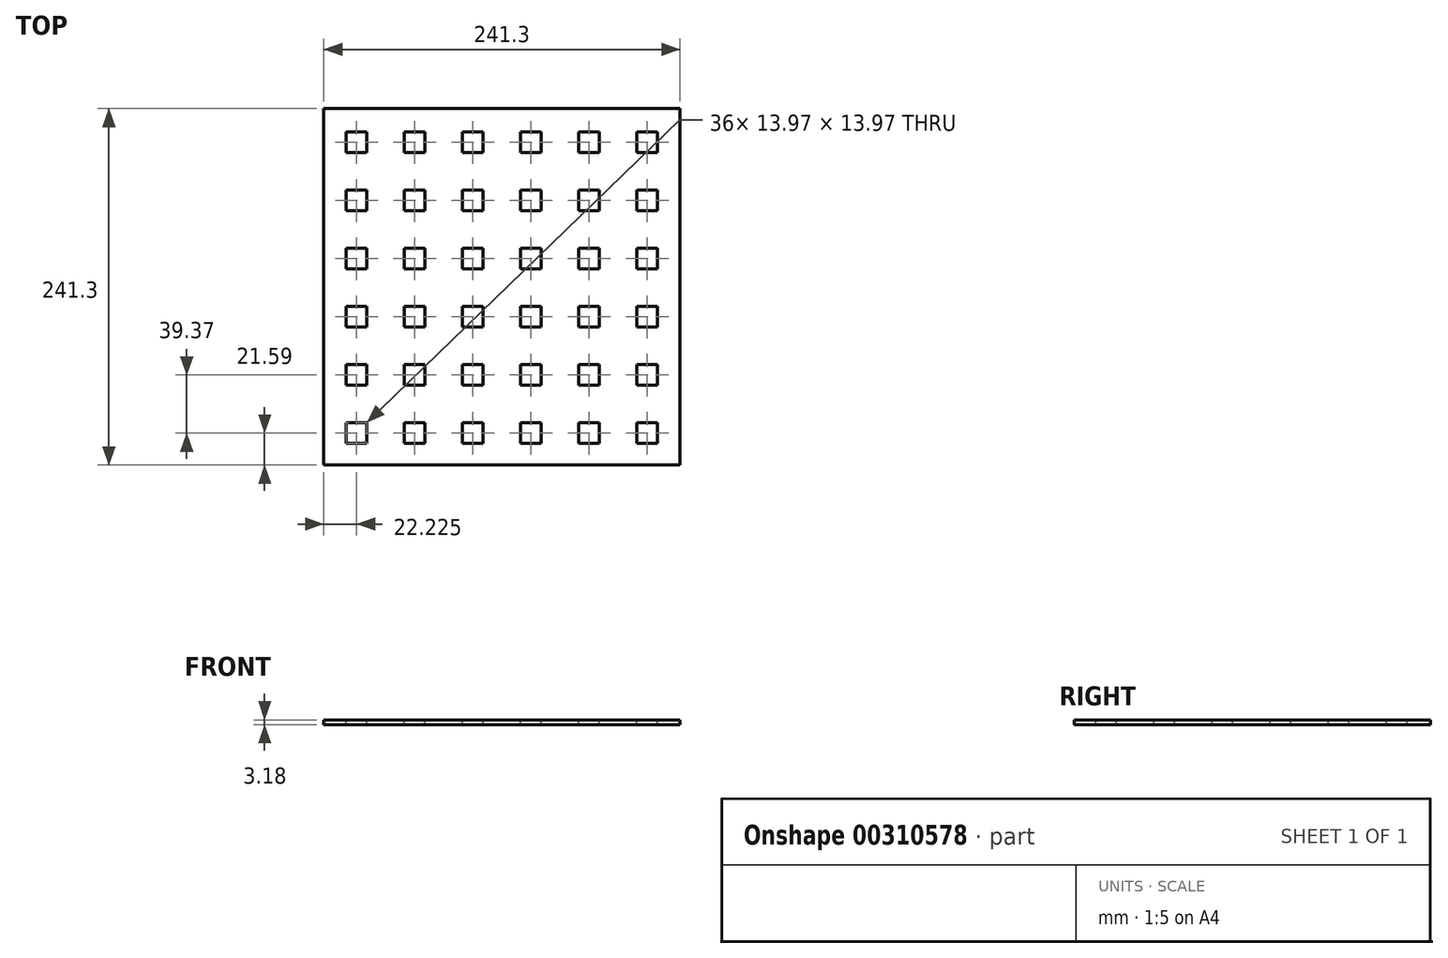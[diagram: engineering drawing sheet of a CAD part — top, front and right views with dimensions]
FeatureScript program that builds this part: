
annotation { "Feature Type Name" : "Feature", "Feature Type Description" : "" }
export const myFeature = defineFeature(function(context is Context, id is Id, definition is map)
    precondition{}
    {
        {
            var Q0;
            Q0=qCreatedBy(makeId("Top.planeOp"),FACE);
            var sketch = newSketch(context, id + "F0", { "sketchPlane" : qUnion([Q0])});
            skLineSegment(sketch, "E0.bottom", {"start": v(120.65, 120.65) * mm, "end": v(-120.65, 120.65) * mm});
            skLineSegment(sketch, "E0.top", {"start": v(120.65, -120.65) * mm, "end": v(-120.65, -120.65) * mm});
            skLineSegment(sketch, "E0.left", {"start": v(120.65, 120.65) * mm, "end": v(120.65, -120.65) * mm});
            skLineSegment(sketch, "E0.right", {"start": v(-120.65, 120.65) * mm, "end": v(-120.65, -120.65) * mm});
            skPoint(sketch, "E0.middle", {"position": v(0, 0) * mm});
            skSolve(sketch);
        }
        {
            var Q0;
            Q0=makeQuery(id+"F0.imprint","IMPRINT",FACE,{"disambiguationData":[TD([[makeQuery(id+"F0.imprint","IMPRINT",EDGE,{"derivedFrom":sQuery(id+"F0.wireOp",EDGE,"E0.bottom")}),1.0]])]});
            extrude(context, id + "F1", {"entities" : qUnion([Q0]), "depth" : 3.17 * mm, "symmetric" : true});
        }
        {
            var Q0;
            Q0=makeQuery(id+"F1.opExtrude","CAP_FACE",FACE,{"disambiguationData":[OSD([sQuery(id+"F0.wireOp",EDGE,"E0.bottom"),sQuery(id+"F0.wireOp",EDGE,"E0.top"),sQuery(id+"F0.wireOp",EDGE,"E0.left"),sQuery(id+"F0.wireOp",EDGE,"E0.right")])],"isStart":false});
            var sketch = newSketch(context, id + "F2", { "sketchPlane" : qUnion([Q0])});
            skLineSegment(sketch, "E1.bottom", {"start": v(-91.44, 104.78) * mm, "end": v(-105.41, 104.78) * mm});
            skLineSegment(sketch, "E1.top", {"start": v(-91.44, 90.8) * mm, "end": v(-105.41, 90.8) * mm});
            skLineSegment(sketch, "E1.left", {"start": v(-91.44, 104.78) * mm, "end": v(-91.44, 90.8) * mm});
            skLineSegment(sketch, "E1.right", {"start": v(-105.41, 104.78) * mm, "end": v(-105.41, 90.8) * mm});
            skPoint(sketch, "E1.middle", {"position": v(-98.43, 97.8) * mm});
            skLineSegment(sketch, "E2.0.1.0", {"start": v(-105.41, 65.4) * mm, "end": v(-105.41, 51.44) * mm});
            skLineSegment(sketch, "E2.0.1.1", {"start": v(-91.44, 65.4) * mm, "end": v(-105.41, 65.4) * mm});
            skLineSegment(sketch, "E2.0.1.2", {"start": v(-91.44, 65.4) * mm, "end": v(-91.44, 51.44) * mm});
            skLineSegment(sketch, "E2.0.1.3", {"start": v(-91.44, 51.44) * mm, "end": v(-105.41, 51.44) * mm});
            skLineSegment(sketch, "E2.0.2.0", {"start": v(-105.41, 26.04) * mm, "end": v(-105.41, 12.07) * mm});
            skLineSegment(sketch, "E2.0.2.1", {"start": v(-91.44, 26.04) * mm, "end": v(-105.41, 26.04) * mm});
            skLineSegment(sketch, "E2.0.2.2", {"start": v(-91.44, 26.04) * mm, "end": v(-91.44, 12.07) * mm});
            skLineSegment(sketch, "E2.0.2.3", {"start": v(-91.44, 12.07) * mm, "end": v(-105.41, 12.07) * mm});
            skLineSegment(sketch, "E2.0.3.0", {"start": v(-105.41, -13.33) * mm, "end": v(-105.41, -27.3) * mm});
            skLineSegment(sketch, "E2.0.3.1", {"start": v(-91.44, -13.33) * mm, "end": v(-105.41, -13.33) * mm});
            skLineSegment(sketch, "E2.0.3.2", {"start": v(-91.44, -13.33) * mm, "end": v(-91.44, -27.3) * mm});
            skLineSegment(sketch, "E2.0.3.3", {"start": v(-91.44, -27.3) * mm, "end": v(-105.41, -27.3) * mm});
            skLineSegment(sketch, "E2.0.4.0", {"start": v(-105.41, -52.7) * mm, "end": v(-105.41, -66.67) * mm});
            skLineSegment(sketch, "E2.0.4.1", {"start": v(-91.44, -52.7) * mm, "end": v(-105.41, -52.7) * mm});
            skLineSegment(sketch, "E2.0.4.2", {"start": v(-91.44, -52.7) * mm, "end": v(-91.44, -66.67) * mm});
            skLineSegment(sketch, "E2.0.4.3", {"start": v(-91.44, -66.67) * mm, "end": v(-105.41, -66.67) * mm});
            skLineSegment(sketch, "E2.0.5.0", {"start": v(-105.41, -92.07) * mm, "end": v(-105.41, -106.04) * mm});
            skLineSegment(sketch, "E2.0.5.1", {"start": v(-91.44, -92.07) * mm, "end": v(-105.41, -92.07) * mm});
            skLineSegment(sketch, "E2.0.5.2", {"start": v(-91.44, -92.07) * mm, "end": v(-91.44, -106.04) * mm});
            skLineSegment(sketch, "E2.0.5.3", {"start": v(-91.44, -106.05) * mm, "end": v(-105.41, -106.05) * mm});
            skLineSegment(sketch, "E2.1.0.0", {"start": v(-66.04, 104.78) * mm, "end": v(-66.04, 90.8) * mm});
            skLineSegment(sketch, "E2.1.0.1", {"start": v(-52.07, 104.78) * mm, "end": v(-66.04, 104.78) * mm});
            skLineSegment(sketch, "E2.1.0.2", {"start": v(-52.07, 104.78) * mm, "end": v(-52.07, 90.8) * mm});
            skLineSegment(sketch, "E2.1.0.3", {"start": v(-52.07, 90.8) * mm, "end": v(-66.04, 90.8) * mm});
            skLineSegment(sketch, "E2.1.1.0", {"start": v(-66.04, 65.4) * mm, "end": v(-66.04, 51.44) * mm});
            skLineSegment(sketch, "E2.1.1.1", {"start": v(-52.07, 65.4) * mm, "end": v(-66.04, 65.4) * mm});
            skLineSegment(sketch, "E2.1.1.2", {"start": v(-52.07, 65.4) * mm, "end": v(-52.07, 51.44) * mm});
            skLineSegment(sketch, "E2.1.1.3", {"start": v(-52.07, 51.44) * mm, "end": v(-66.04, 51.44) * mm});
            skLineSegment(sketch, "E2.1.2.0", {"start": v(-66.04, 26.04) * mm, "end": v(-66.04, 12.07) * mm});
            skLineSegment(sketch, "E2.1.2.1", {"start": v(-52.07, 26.04) * mm, "end": v(-66.04, 26.04) * mm});
            skLineSegment(sketch, "E2.1.2.2", {"start": v(-52.07, 26.04) * mm, "end": v(-52.07, 12.07) * mm});
            skLineSegment(sketch, "E2.1.2.3", {"start": v(-52.07, 12.07) * mm, "end": v(-66.04, 12.07) * mm});
            skLineSegment(sketch, "E2.1.3.0", {"start": v(-66.04, -13.33) * mm, "end": v(-66.04, -27.3) * mm});
            skLineSegment(sketch, "E2.1.3.1", {"start": v(-52.07, -13.33) * mm, "end": v(-66.04, -13.33) * mm});
            skLineSegment(sketch, "E2.1.3.2", {"start": v(-52.07, -13.33) * mm, "end": v(-52.07, -27.3) * mm});
            skLineSegment(sketch, "E2.1.3.3", {"start": v(-52.07, -27.3) * mm, "end": v(-66.04, -27.3) * mm});
            skLineSegment(sketch, "E2.1.4.0", {"start": v(-66.04, -52.7) * mm, "end": v(-66.04, -66.67) * mm});
            skLineSegment(sketch, "E2.1.4.1", {"start": v(-52.07, -52.7) * mm, "end": v(-66.04, -52.7) * mm});
            skLineSegment(sketch, "E2.1.4.2", {"start": v(-52.07, -52.7) * mm, "end": v(-52.07, -66.67) * mm});
            skLineSegment(sketch, "E2.1.4.3", {"start": v(-52.07, -66.67) * mm, "end": v(-66.04, -66.67) * mm});
            skLineSegment(sketch, "E2.1.5.0", {"start": v(-66.04, -92.07) * mm, "end": v(-66.04, -106.04) * mm});
            skLineSegment(sketch, "E2.1.5.1", {"start": v(-52.07, -92.07) * mm, "end": v(-66.04, -92.07) * mm});
            skLineSegment(sketch, "E2.1.5.2", {"start": v(-52.07, -92.07) * mm, "end": v(-52.07, -106.04) * mm});
            skLineSegment(sketch, "E2.1.5.3", {"start": v(-52.07, -106.05) * mm, "end": v(-66.04, -106.05) * mm});
            skLineSegment(sketch, "E2.2.0.0", {"start": v(-26.67, 104.78) * mm, "end": v(-26.67, 90.8) * mm});
            skLineSegment(sketch, "E2.2.0.1", {"start": v(-12.7, 104.78) * mm, "end": v(-26.67, 104.78) * mm});
            skLineSegment(sketch, "E2.2.0.2", {"start": v(-12.7, 104.78) * mm, "end": v(-12.7, 90.8) * mm});
            skLineSegment(sketch, "E2.2.0.3", {"start": v(-12.7, 90.8) * mm, "end": v(-26.67, 90.8) * mm});
            skLineSegment(sketch, "E2.2.1.0", {"start": v(-26.67, 65.4) * mm, "end": v(-26.67, 51.44) * mm});
            skLineSegment(sketch, "E2.2.1.1", {"start": v(-12.7, 65.4) * mm, "end": v(-26.67, 65.4) * mm});
            skLineSegment(sketch, "E2.2.1.2", {"start": v(-12.7, 65.4) * mm, "end": v(-12.7, 51.44) * mm});
            skLineSegment(sketch, "E2.2.1.3", {"start": v(-12.7, 51.44) * mm, "end": v(-26.67, 51.44) * mm});
            skLineSegment(sketch, "E2.2.2.0", {"start": v(-26.67, 26.04) * mm, "end": v(-26.67, 12.07) * mm});
            skLineSegment(sketch, "E2.2.2.1", {"start": v(-12.7, 26.04) * mm, "end": v(-26.67, 26.04) * mm});
            skLineSegment(sketch, "E2.2.2.2", {"start": v(-12.7, 26.04) * mm, "end": v(-12.7, 12.07) * mm});
            skLineSegment(sketch, "E2.2.2.3", {"start": v(-12.7, 12.07) * mm, "end": v(-26.67, 12.07) * mm});
            skLineSegment(sketch, "E2.2.3.0", {"start": v(-26.67, -13.33) * mm, "end": v(-26.67, -27.3) * mm});
            skLineSegment(sketch, "E2.2.3.1", {"start": v(-12.7, -13.33) * mm, "end": v(-26.67, -13.33) * mm});
            skLineSegment(sketch, "E2.2.3.2", {"start": v(-12.7, -13.33) * mm, "end": v(-12.7, -27.3) * mm});
            skLineSegment(sketch, "E2.2.3.3", {"start": v(-12.7, -27.3) * mm, "end": v(-26.67, -27.3) * mm});
            skLineSegment(sketch, "E2.2.4.0", {"start": v(-26.67, -52.7) * mm, "end": v(-26.67, -66.67) * mm});
            skLineSegment(sketch, "E2.2.4.1", {"start": v(-12.7, -52.7) * mm, "end": v(-26.67, -52.7) * mm});
            skLineSegment(sketch, "E2.2.4.2", {"start": v(-12.7, -52.7) * mm, "end": v(-12.7, -66.67) * mm});
            skLineSegment(sketch, "E2.2.4.3", {"start": v(-12.7, -66.67) * mm, "end": v(-26.67, -66.67) * mm});
            skLineSegment(sketch, "E2.2.5.0", {"start": v(-26.67, -92.07) * mm, "end": v(-26.67, -106.04) * mm});
            skLineSegment(sketch, "E2.2.5.1", {"start": v(-12.7, -92.07) * mm, "end": v(-26.67, -92.07) * mm});
            skLineSegment(sketch, "E2.2.5.2", {"start": v(-12.7, -92.07) * mm, "end": v(-12.7, -106.04) * mm});
            skLineSegment(sketch, "E2.2.5.3", {"start": v(-12.7, -106.05) * mm, "end": v(-26.67, -106.05) * mm});
            skLineSegment(sketch, "E2.3.0.0", {"start": v(12.7, 104.78) * mm, "end": v(12.7, 90.8) * mm});
            skLineSegment(sketch, "E2.3.0.1", {"start": v(26.67, 104.78) * mm, "end": v(12.7, 104.78) * mm});
            skLineSegment(sketch, "E2.3.0.2", {"start": v(26.67, 104.78) * mm, "end": v(26.67, 90.8) * mm});
            skLineSegment(sketch, "E2.3.0.3", {"start": v(26.67, 90.8) * mm, "end": v(12.7, 90.8) * mm});
            skLineSegment(sketch, "E2.3.1.0", {"start": v(12.7, 65.4) * mm, "end": v(12.7, 51.44) * mm});
            skLineSegment(sketch, "E2.3.1.1", {"start": v(26.67, 65.4) * mm, "end": v(12.7, 65.4) * mm});
            skLineSegment(sketch, "E2.3.1.2", {"start": v(26.67, 65.4) * mm, "end": v(26.67, 51.44) * mm});
            skLineSegment(sketch, "E2.3.1.3", {"start": v(26.67, 51.44) * mm, "end": v(12.7, 51.44) * mm});
            skLineSegment(sketch, "E2.3.2.0", {"start": v(12.7, 26.04) * mm, "end": v(12.7, 12.07) * mm});
            skLineSegment(sketch, "E2.3.2.1", {"start": v(26.67, 26.04) * mm, "end": v(12.7, 26.04) * mm});
            skLineSegment(sketch, "E2.3.2.2", {"start": v(26.67, 26.04) * mm, "end": v(26.67, 12.07) * mm});
            skLineSegment(sketch, "E2.3.2.3", {"start": v(26.67, 12.07) * mm, "end": v(12.7, 12.07) * mm});
            skLineSegment(sketch, "E2.3.3.0", {"start": v(12.7, -13.33) * mm, "end": v(12.7, -27.3) * mm});
            skLineSegment(sketch, "E2.3.3.1", {"start": v(26.67, -13.33) * mm, "end": v(12.7, -13.33) * mm});
            skLineSegment(sketch, "E2.3.3.2", {"start": v(26.67, -13.33) * mm, "end": v(26.67, -27.3) * mm});
            skLineSegment(sketch, "E2.3.3.3", {"start": v(26.67, -27.3) * mm, "end": v(12.7, -27.3) * mm});
            skLineSegment(sketch, "E2.3.4.0", {"start": v(12.7, -52.7) * mm, "end": v(12.7, -66.67) * mm});
            skLineSegment(sketch, "E2.3.4.1", {"start": v(26.67, -52.7) * mm, "end": v(12.7, -52.7) * mm});
            skLineSegment(sketch, "E2.3.4.2", {"start": v(26.67, -52.7) * mm, "end": v(26.67, -66.67) * mm});
            skLineSegment(sketch, "E2.3.4.3", {"start": v(26.67, -66.67) * mm, "end": v(12.7, -66.67) * mm});
            skLineSegment(sketch, "E2.3.5.0", {"start": v(12.7, -92.07) * mm, "end": v(12.7, -106.04) * mm});
            skLineSegment(sketch, "E2.3.5.1", {"start": v(26.67, -92.07) * mm, "end": v(12.7, -92.07) * mm});
            skLineSegment(sketch, "E2.3.5.2", {"start": v(26.67, -92.07) * mm, "end": v(26.67, -106.04) * mm});
            skLineSegment(sketch, "E2.3.5.3", {"start": v(26.67, -106.05) * mm, "end": v(12.7, -106.05) * mm});
            skLineSegment(sketch, "E2.4.0.0", {"start": v(52.07, 104.78) * mm, "end": v(52.07, 90.8) * mm});
            skLineSegment(sketch, "E2.4.0.1", {"start": v(66.04, 104.78) * mm, "end": v(52.07, 104.78) * mm});
            skLineSegment(sketch, "E2.4.0.2", {"start": v(66.04, 104.78) * mm, "end": v(66.04, 90.8) * mm});
            skLineSegment(sketch, "E2.4.0.3", {"start": v(66.04, 90.8) * mm, "end": v(52.07, 90.8) * mm});
            skLineSegment(sketch, "E2.4.1.0", {"start": v(52.07, 65.4) * mm, "end": v(52.07, 51.44) * mm});
            skLineSegment(sketch, "E2.4.1.1", {"start": v(66.04, 65.4) * mm, "end": v(52.07, 65.4) * mm});
            skLineSegment(sketch, "E2.4.1.2", {"start": v(66.04, 65.4) * mm, "end": v(66.04, 51.44) * mm});
            skLineSegment(sketch, "E2.4.1.3", {"start": v(66.04, 51.44) * mm, "end": v(52.07, 51.44) * mm});
            skLineSegment(sketch, "E2.4.2.0", {"start": v(52.07, 26.04) * mm, "end": v(52.07, 12.07) * mm});
            skLineSegment(sketch, "E2.4.2.1", {"start": v(66.04, 26.04) * mm, "end": v(52.07, 26.04) * mm});
            skLineSegment(sketch, "E2.4.2.2", {"start": v(66.04, 26.04) * mm, "end": v(66.04, 12.07) * mm});
            skLineSegment(sketch, "E2.4.2.3", {"start": v(66.04, 12.07) * mm, "end": v(52.07, 12.07) * mm});
            skLineSegment(sketch, "E2.4.3.0", {"start": v(52.07, -13.33) * mm, "end": v(52.07, -27.3) * mm});
            skLineSegment(sketch, "E2.4.3.1", {"start": v(66.04, -13.33) * mm, "end": v(52.07, -13.33) * mm});
            skLineSegment(sketch, "E2.4.3.2", {"start": v(66.04, -13.33) * mm, "end": v(66.04, -27.3) * mm});
            skLineSegment(sketch, "E2.4.3.3", {"start": v(66.04, -27.3) * mm, "end": v(52.07, -27.3) * mm});
            skLineSegment(sketch, "E2.4.4.0", {"start": v(52.07, -52.7) * mm, "end": v(52.07, -66.67) * mm});
            skLineSegment(sketch, "E2.4.4.1", {"start": v(66.04, -52.7) * mm, "end": v(52.07, -52.7) * mm});
            skLineSegment(sketch, "E2.4.4.2", {"start": v(66.04, -52.7) * mm, "end": v(66.04, -66.67) * mm});
            skLineSegment(sketch, "E2.4.4.3", {"start": v(66.04, -66.67) * mm, "end": v(52.07, -66.67) * mm});
            skLineSegment(sketch, "E2.4.5.0", {"start": v(52.07, -92.07) * mm, "end": v(52.07, -106.04) * mm});
            skLineSegment(sketch, "E2.4.5.1", {"start": v(66.04, -92.07) * mm, "end": v(52.07, -92.07) * mm});
            skLineSegment(sketch, "E2.4.5.2", {"start": v(66.04, -92.07) * mm, "end": v(66.04, -106.04) * mm});
            skLineSegment(sketch, "E2.4.5.3", {"start": v(66.04, -106.05) * mm, "end": v(52.07, -106.05) * mm});
            skLineSegment(sketch, "E2.5.0.0", {"start": v(91.44, 104.78) * mm, "end": v(91.44, 90.8) * mm});
            skLineSegment(sketch, "E2.5.0.1", {"start": v(105.4, 104.78) * mm, "end": v(91.44, 104.78) * mm});
            skLineSegment(sketch, "E2.5.0.2", {"start": v(105.4, 104.78) * mm, "end": v(105.4, 90.8) * mm});
            skLineSegment(sketch, "E2.5.0.3", {"start": v(105.4, 90.8) * mm, "end": v(91.44, 90.8) * mm});
            skLineSegment(sketch, "E2.5.1.0", {"start": v(91.44, 65.4) * mm, "end": v(91.44, 51.44) * mm});
            skLineSegment(sketch, "E2.5.1.1", {"start": v(105.4, 65.4) * mm, "end": v(91.44, 65.4) * mm});
            skLineSegment(sketch, "E2.5.1.2", {"start": v(105.4, 65.4) * mm, "end": v(105.4, 51.44) * mm});
            skLineSegment(sketch, "E2.5.1.3", {"start": v(105.4, 51.44) * mm, "end": v(91.44, 51.44) * mm});
            skLineSegment(sketch, "E2.5.2.0", {"start": v(91.44, 26.04) * mm, "end": v(91.44, 12.07) * mm});
            skLineSegment(sketch, "E2.5.2.1", {"start": v(105.4, 26.04) * mm, "end": v(91.44, 26.04) * mm});
            skLineSegment(sketch, "E2.5.2.2", {"start": v(105.41, 26.04) * mm, "end": v(105.41, 12.07) * mm});
            skLineSegment(sketch, "E2.5.2.3", {"start": v(105.4, 12.07) * mm, "end": v(91.44, 12.07) * mm});
            skLineSegment(sketch, "E2.5.3.0", {"start": v(91.44, -13.33) * mm, "end": v(91.44, -27.3) * mm});
            skLineSegment(sketch, "E2.5.3.1", {"start": v(105.41, -13.33) * mm, "end": v(91.44, -13.33) * mm});
            skLineSegment(sketch, "E2.5.3.2", {"start": v(105.41, -13.33) * mm, "end": v(105.41, -27.3) * mm});
            skLineSegment(sketch, "E2.5.3.3", {"start": v(105.41, -27.3) * mm, "end": v(91.44, -27.3) * mm});
            skLineSegment(sketch, "E2.5.4.0", {"start": v(91.44, -52.7) * mm, "end": v(91.44, -66.67) * mm});
            skLineSegment(sketch, "E2.5.4.1", {"start": v(105.41, -52.7) * mm, "end": v(91.44, -52.7) * mm});
            skLineSegment(sketch, "E2.5.4.2", {"start": v(105.41, -52.7) * mm, "end": v(105.41, -66.67) * mm});
            skLineSegment(sketch, "E2.5.4.3", {"start": v(105.41, -66.67) * mm, "end": v(91.44, -66.67) * mm});
            skLineSegment(sketch, "E2.5.5.0", {"start": v(91.44, -92.07) * mm, "end": v(91.44, -106.04) * mm});
            skLineSegment(sketch, "E2.5.5.1", {"start": v(105.41, -92.07) * mm, "end": v(91.44, -92.07) * mm});
            skLineSegment(sketch, "E2.5.5.2", {"start": v(105.41, -92.07) * mm, "end": v(105.41, -106.04) * mm});
            skLineSegment(sketch, "E2.5.5.3", {"start": v(105.41, -106.05) * mm, "end": v(91.44, -106.05) * mm});
            skSolve(sketch);
        }
        {
            var Q0;
            Q0 = qSketchRegion(id + "F2", true);
            var Q1;
            Q1=makeQuery(id+"F1.opExtrude","CAP_FACE",FACE,{"disambiguationData":[OSD([sQuery(id+"F0.wireOp",EDGE,"E0.bottom"),sQuery(id+"F0.wireOp",EDGE,"E0.top"),sQuery(id+"F0.wireOp",EDGE,"E0.left"),sQuery(id+"F0.wireOp",EDGE,"E0.right")])],"isStart":true});
            extrude(context, id + "F3", {"entities" : qUnion([Q0]), "operationType" : NewBodyOperationType.REMOVE, "endBound" : BoundingType.UP_TO_SURFACE, "oppositeDirection" : true, "endBoundEntityFace" : qUnion([Q1]), "depth" : 25.4 * mm});
        }
    });
